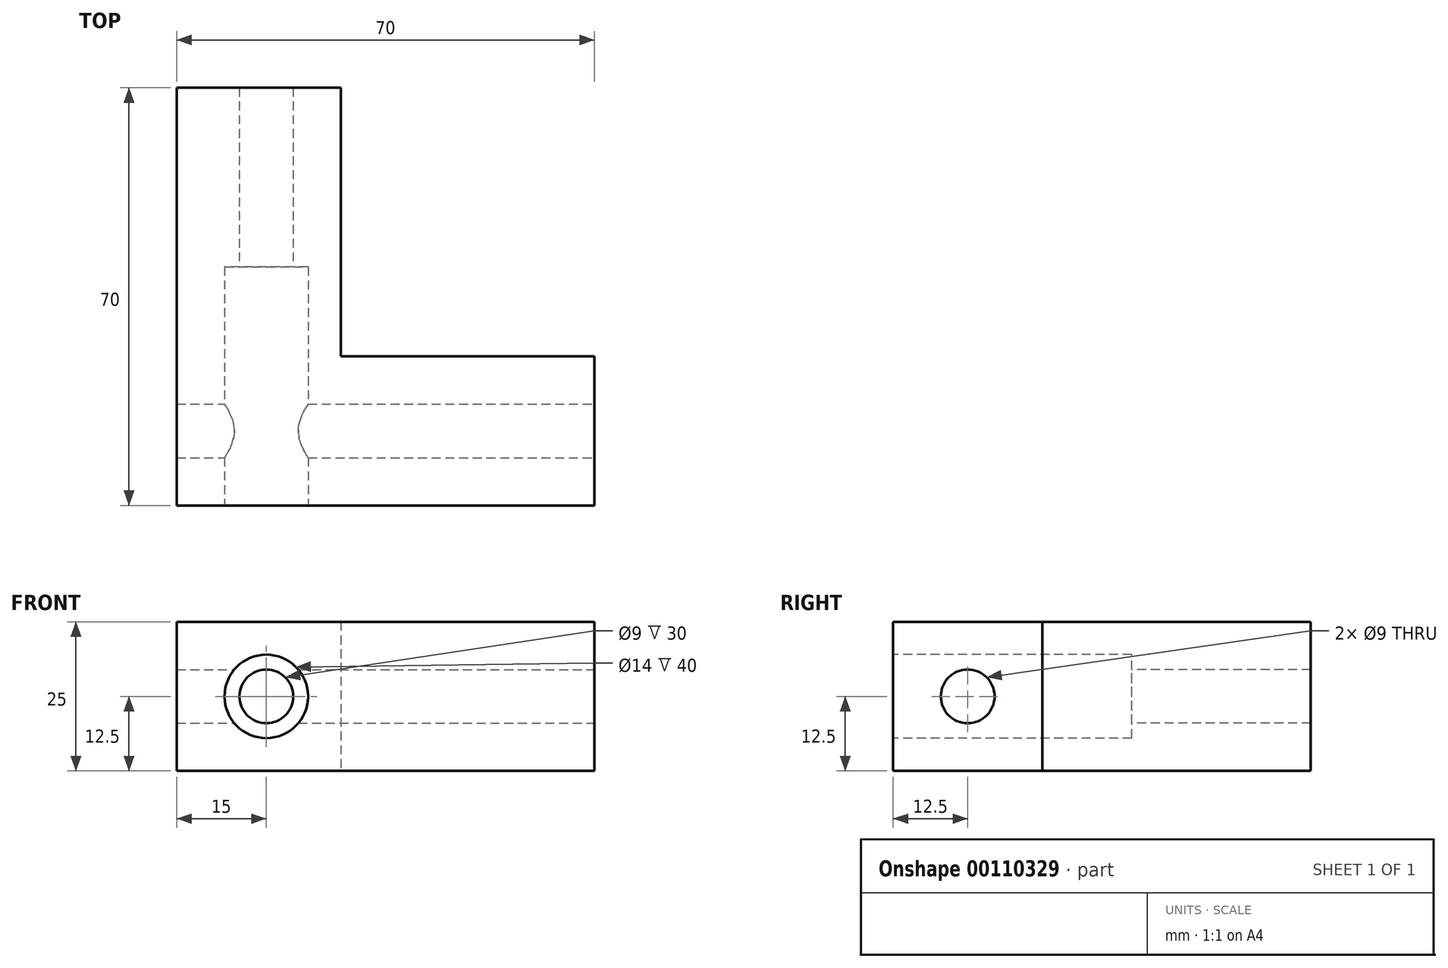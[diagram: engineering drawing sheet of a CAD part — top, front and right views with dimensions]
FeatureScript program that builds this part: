
annotation { "Feature Type Name" : "Feature", "Feature Type Description" : "" }
export const myFeature = defineFeature(function(context is Context, id is Id, definition is map)
    precondition{}
    {
        {
            var Q0;
            Q0=qCreatedBy(makeId("Front.planeOp"),FACE);
            var sketch = newSketch(context, id + "F0", { "sketchPlane" : qUnion([Q0])});
            skLineSegment(sketch, "E0.bottom", {"start": v(35, 12.5) * mm, "end": v(-35, 12.5) * mm});
            skLineSegment(sketch, "E0.top", {"start": v(35, -12.5) * mm, "end": v(-35, -12.5) * mm});
            skLineSegment(sketch, "E0.left", {"start": v(35, 12.5) * mm, "end": v(35, -12.5) * mm});
            skLineSegment(sketch, "E0.right", {"start": v(-35, 12.5) * mm, "end": v(-35, -12.5) * mm});
            skPoint(sketch, "E0.middle", {"position": v(0, 0) * mm});
            skCircle(sketch, "E1", {"center": v(-20, 0) * mm, "radius": 4.5 * mm});
            skCircle(sketch, "E2", {"center": v(-20, 0) * mm, "radius": 7 * mm});
            skLineSegment(sketch, "E3.bottom", {"start": v(-7.5, 12.5) * mm, "end": v(-32.5, 12.5) * mm});
            skLineSegment(sketch, "E3.top", {"start": v(-7.5, -12.5) * mm, "end": v(-32.5, -12.5) * mm});
            skLineSegment(sketch, "E3.left", {"start": v(-7.5, 12.5) * mm, "end": v(-7.5, -12.5) * mm});
            skLineSegment(sketch, "E3.right", {"start": v(-32.5, 12.5) * mm, "end": v(-32.5, -12.5) * mm});
            skSolve(sketch);
        }
        {
            var Q0;
            {var subQ0=sQuery(id+"F0.wireOp",EDGE,"E0.right");Q0=makeQuery(id+"F0.imprint","IMPRINT",FACE,{"disambiguationData":[TD([[makeQuery(id+"F0.imprint","IMPRINT",EDGE,{"derivedFrom":subQ0}),1.0]])]});}
            var Q1;
            Q1=makeQuery(id+"F0.imprint","IMPRINT",FACE,{"disambiguationData":[TD([[makeQuery(id+"F0.imprint","IMPRINT",EDGE,{"derivedFrom":sQuery(id+"F0.wireOp",EDGE,"E1")}),-1.0]])]});
            var Q2;
            Q2=makeQuery(id+"F0.imprint","IMPRINT",FACE,{"disambiguationData":[TD([[makeQuery(id+"F0.imprint","IMPRINT",EDGE,{"derivedFrom":sQuery(id+"F0.wireOp",EDGE,"E2")}),-1.0]])]});
            extrude(context, id + "F1", {"entities" : qUnion([Q0, Q1, Q2]), "oppositeDirection" : true, "depth" : 70 * mm});
        }
        {
            var Q0;
            Q0=makeQuery(id+"F0.imprint","IMPRINT",FACE,{"disambiguationData":[TD([[makeQuery(id+"F0.imprint","IMPRINT",EDGE,{"derivedFrom":sQuery(id+"F0.wireOp",EDGE,"E1")}),-1.0]])]});
            extrude(context, id + "F2", {"entities" : qUnion([Q0]), "operationType" : NewBodyOperationType.REMOVE, "oppositeDirection" : true, "depth" : 40 * mm});
        }
        {
            var Q0;
            {var subQ0=sQuery(id+"F0.wireOp",EDGE,"E0.left");Q0=makeQuery(id+"F0.imprint","IMPRINT",FACE,{"disambiguationData":[TD([[makeQuery(id+"F0.imprint","IMPRINT",EDGE,{"derivedFrom":subQ0}),-1.0]])]});}
            extrude(context, id + "F3", {"entities" : qUnion([Q0]), "operationType" : NewBodyOperationType.ADD, "oppositeDirection" : true, "depth" : 25 * mm});
        }
        {
            var Q0;
            Q0=makeQuery(id+"F3.opExtrude","SWEPT_FACE",FACE,{"disambiguationData":[OSD([sQuery(id+"F0.wireOp",EDGE,"E0.left")])]});
            var sketch = newSketch(context, id + "F4", { "sketchPlane" : qUnion([Q0])});
            skCircle(sketch, "E4", {"center": v(12.5, 0) * mm, "radius": 4.5 * mm});
            skCircle(sketch, "E5", {"center": v(12.5, 0) * mm, "radius": 12.5 * mm});
            skSolve(sketch);
        }
        {
            var Q0;
            Q0=makeQuery(id+"F4.imprint","IMPRINT",FACE,{"disambiguationData":[TD([[makeQuery(id+"F4.imprint","IMPRINT",EDGE,{"derivedFrom":sQuery(id+"F4.wireOp",EDGE,"E4")}),1.0]])]});
            extrude(context, id + "F5", {"entities" : qUnion([Q0]), "operationType" : NewBodyOperationType.REMOVE, "endBound" : BoundingType.THROUGH_ALL, "oppositeDirection" : true, "depth" : 25 * mm});
        }
    });
